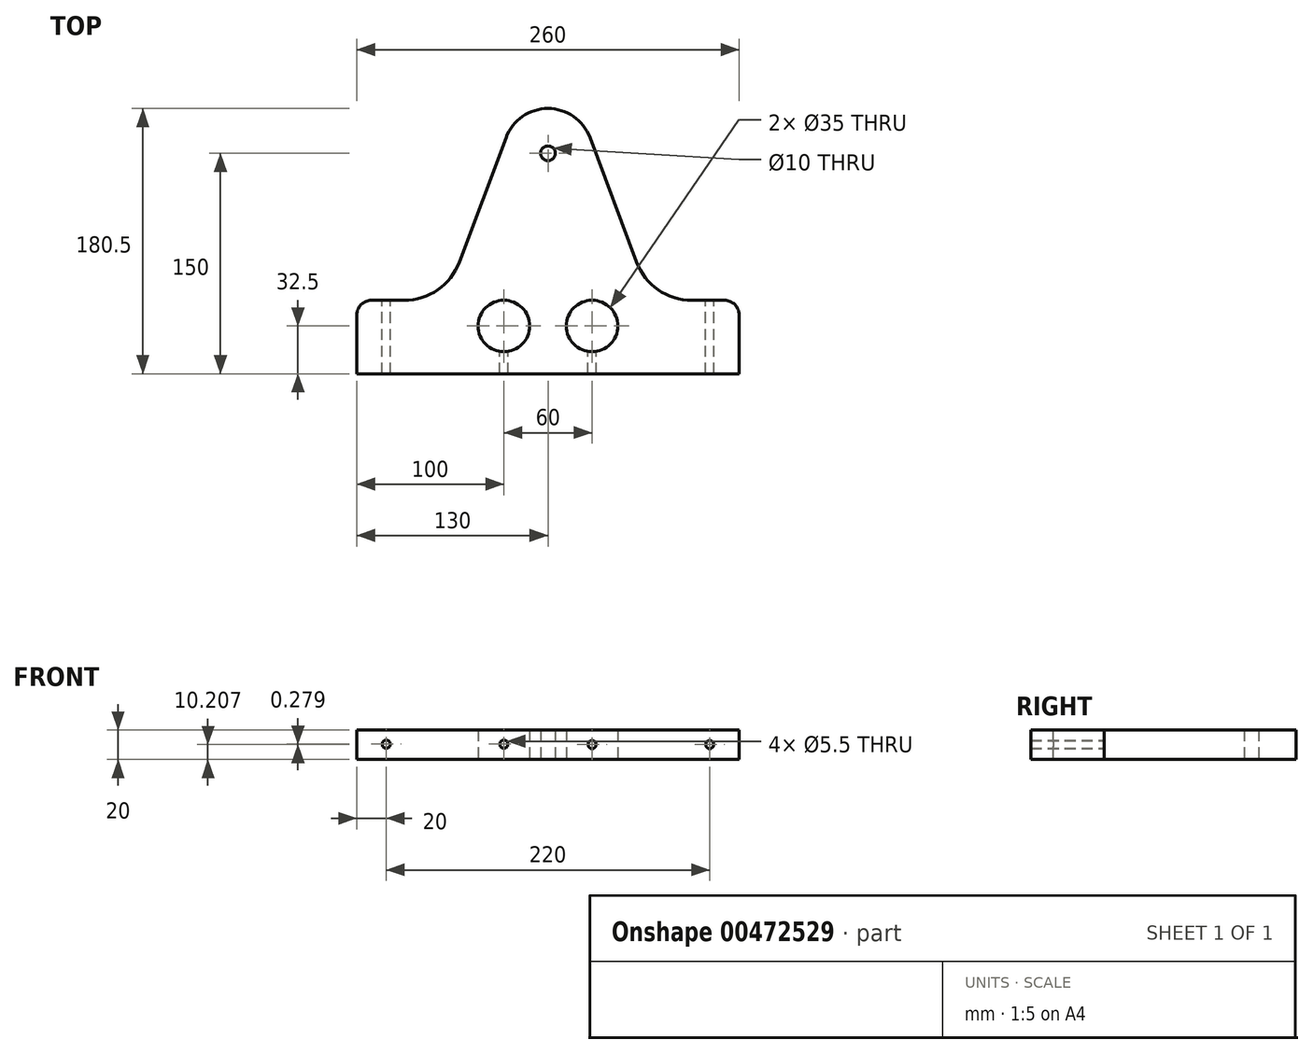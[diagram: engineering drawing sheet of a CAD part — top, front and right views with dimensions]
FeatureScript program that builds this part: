
annotation { "Feature Type Name" : "Feature", "Feature Type Description" : "" }
export const myFeature = defineFeature(function(context is Context, id is Id, definition is map)
    precondition{}
    {
        {
            var Q0;
            Q0=qCreatedBy(makeId("Top.planeOp"),FACE);
            var sketch = newSketch(context, id + "F0", { "sketchPlane" : qUnion([Q0])});
            skLineSegment(sketch, "E0.bottom", {"start": v(130, 0) * mm, "end": v(-130, 0) * mm});
            skLineSegment(sketch, "E0.left", {"start": v(130, 0) * mm, "end": v(130, 50) * mm});
            skLineSegment(sketch, "E0.right", {"start": v(-130, 0) * mm, "end": v(-130, 50) * mm});
            skPoint(sketch, "E0.middle", {"position": v(0, 56.15) * mm});
            skArc(sketch, "E1", {"start": v(28.56, 160.7) * mm, "mid": v(0, 180.5) * mm, "end": v(-28.56, 160.7) * mm});
            skLineSegment(sketch, "E2", {"start": v(-130, 50) * mm, "end": v(-70, 50) * mm});
            skLineSegment(sketch, "E3", {"start": v(-70, 50) * mm, "end": v(-28.56, 160.7) * mm});
            skLineSegment(sketch, "E4", {"start": v(130, 50) * mm, "end": v(70, 50) * mm});
            skLineSegment(sketch, "E5", {"start": v(70, 50) * mm, "end": v(28.56, 160.7) * mm});
            skPoint(sketch, "E6.orphan", {"position": v(130, 112.3) * mm});
            skPoint(sketch, "E7.orphan", {"position": v(-130, 112.3) * mm});
            skCircle(sketch, "E8", {"center": v(0, 150) * mm, "radius": 5 * mm});
            skCircle(sketch, "E9", {"center": v(30, 32.5) * mm, "radius": 17.5 * mm});
            skCircle(sketch, "E10", {"center": v(-30, 32.5) * mm, "radius": 17.5 * mm});
            skSolve(sketch);
        }
        {
            var Q0;
            Q0=makeQuery(id+"F0.imprint","IMPRINT",FACE,{"disambiguationData":[TD([[makeQuery(id+"F0.imprint","IMPRINT",EDGE,{"derivedFrom":sQuery(id+"F0.wireOp",EDGE,"E0.bottom")}),-1.0]])]});
            extrude(context, id + "F1", {"entities" : qUnion([Q0]), "depth" : 20 * mm});
        }
        {
            var Q0;
            Q0=makeQuery(id+"F1.opExtrude","SWEPT_FACE",FACE,{"disambiguationData":[OSD([sQuery(id+"F0.wireOp",EDGE,"E2")])]});
            var sketch = newSketch(context, id + "F2", { "sketchPlane" : qUnion([Q0])});
            skCircle(sketch, "E11", {"center": v(-110, 10.2) * mm, "radius": 2.75 * mm});
            skCircle(sketch, "E12", {"center": v(110, 10.49) * mm, "radius": 2.75 * mm});
            skCircle(sketch, "E13", {"center": v(-30, 10.2) * mm, "radius": 2.75 * mm});
            skCircle(sketch, "E14", {"center": v(30, 10.49) * mm, "radius": 2.75 * mm});
            skSolve(sketch);
        }
        {
            var Q0;
            Q0 = qSketchRegion(id + "F2", true);
            extrude(context, id + "F3", {"entities" : qUnion([Q0]), "operationType" : NewBodyOperationType.REMOVE, "endBound" : BoundingType.THROUGH_ALL, "oppositeDirection" : true, "depth" : 25 * mm});
        }
        {
            var Q0;
            Q0=makeQuery(id+"F1.opExtrude","SWEPT_EDGE",EDGE,{"disambiguationData":[OSD([sQuery(id+"F0.wireOp",EDGE,"E4"),sQuery(id+"F0.wireOp",EDGE,"E5")])]});
            var Q1;
            Q1=makeQuery(id+"F1.opExtrude","SWEPT_EDGE",EDGE,{"disambiguationData":[OSD([sQuery(id+"F0.wireOp",EDGE,"E2"),sQuery(id+"F0.wireOp",EDGE,"E3")])]});
            fillet(context, id + "F4", {"entities" : qUnion([Q0, Q1]), "radius" : 40 * mm, "tangentPropagation" : true, "allowEdgeOverflow" : false});
        }
        {
            var Q0;
            Q0=makeQuery(id+"F1.opExtrude","SWEPT_EDGE",EDGE,{"disambiguationData":[OSD([sQuery(id+"F0.wireOp",EDGE,"E0.left"),sQuery(id+"F0.wireOp",EDGE,"E4")])]});
            var Q1;
            Q1=makeQuery(id+"F1.opExtrude","SWEPT_EDGE",EDGE,{"disambiguationData":[OSD([sQuery(id+"F0.wireOp",EDGE,"E0.right"),sQuery(id+"F0.wireOp",EDGE,"E2")])]});
            fillet(context, id + "F5", {"entities" : qUnion([Q0, Q1]), "radius" : 10 * mm, "tangentPropagation" : true, "allowEdgeOverflow" : false});
        }
    });
